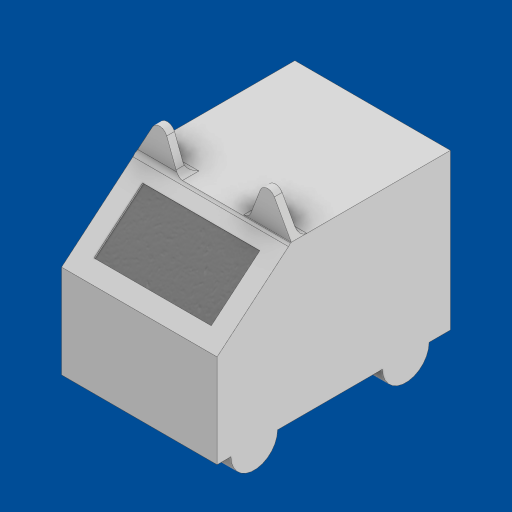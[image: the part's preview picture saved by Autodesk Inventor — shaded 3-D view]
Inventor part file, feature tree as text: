
AUTODESK INVENTOR PART (.ipt)
format: ipt  version: 2023.1 (Build 271208000, 208)  size: 184,832 bytes
history: native  units: mm
features: extrude x5, sketch x5, plane x2, mirror x1, chamfer x1, fillet x1
ambient origin geometry x8: Origin, YZ Plane, XZ Plane, XY Plane, X Axis, Y Axis, Z Axis, Center Point
bodies: Solid1 (feature_tree)
feature tree (15):
  extrude  "Extrusion1"  Depth=100.0mm
  extrude  "Extrusion2"  Depth=50.0mm
  sketch  "Sketch3"  dims[d4=150.0mm d5=0.0mm d6=80.0mm d7=-2.617994mm]
  plane  "Work Plane1"
  extrude  "Extrusion3"  Depth=80.0mm
  mirror  "Mirror1"
  chamfer  "Chamfer1"  Distance=10.0mm
  extrude  "Extrusion4"  Depth=5.0mm
  plane  "Work Plane2"
  extrude  "Extrusion5"  Depth=5.0mm TaperAngle=0.0deg
  fillet  "Fillet1"  Radius=5.0mm
  sketch  "Sketch1"  dims[d0=100.0mm d1=100.0mm]
  sketch  "Sketch2"  dims[d2=50.0mm d3=50.0mm]
  sketch  "Sketch4"  dims[d8=30.0mm]
  sketch  "Sketch5"  dims[d9=30.0mm d10=10.0mm d11=0.0mm d12=40.0mm d13=2.0mm d14=8.726646mm d15=1.0mm d16=0.0mm d17=5.0mm d18=0.0mm d19=5.0mm]
